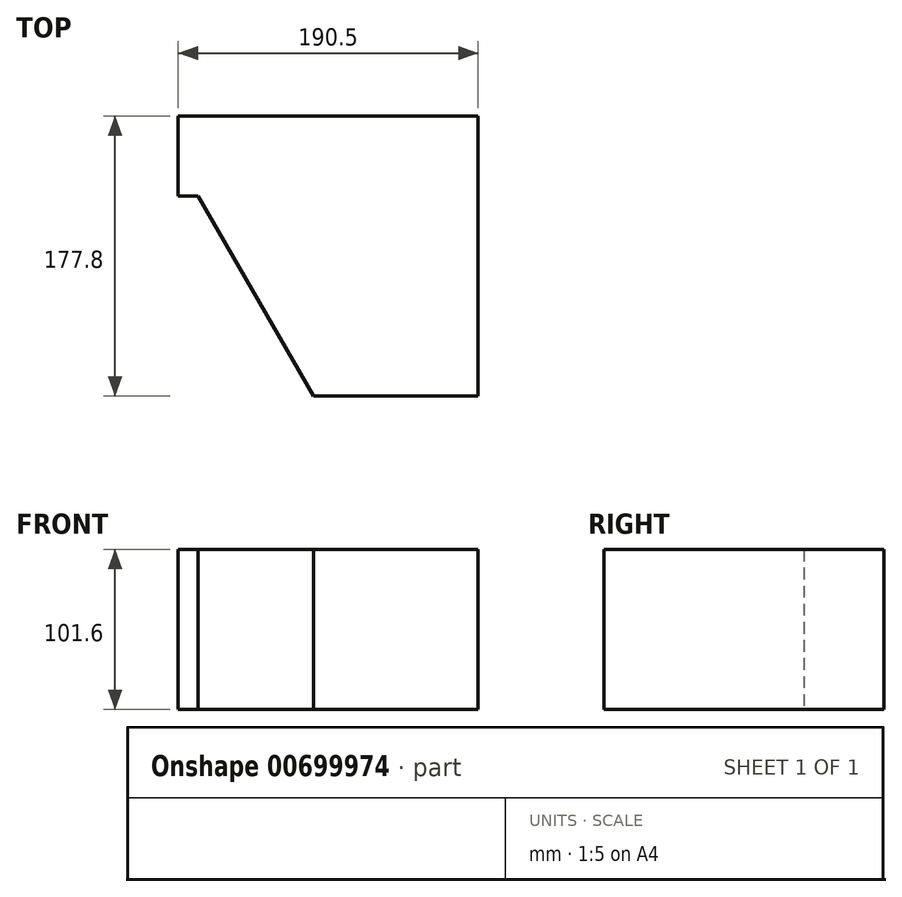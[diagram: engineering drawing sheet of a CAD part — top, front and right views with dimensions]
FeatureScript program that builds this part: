
annotation { "Feature Type Name" : "Feature", "Feature Type Description" : "" }
export const myFeature = defineFeature(function(context is Context, id is Id, definition is map)
    precondition{}
    {
        {
            var Q0;
            Q0=qCreatedBy(makeId("Front.planeOp"),FACE);
            var sketch = newSketch(context, id + "F0", { "sketchPlane" : qUnion([Q0])});
            skLineSegment(sketch, "E0.bottom", {"start": v(-95.25, 50.8) * mm, "end": v(95.25, 50.8) * mm});
            skLineSegment(sketch, "E0.top", {"start": v(-95.25, -50.8) * mm, "end": v(95.25, -50.8) * mm});
            skLineSegment(sketch, "E0.left", {"start": v(-95.25, 50.8) * mm, "end": v(-95.25, -50.8) * mm});
            skLineSegment(sketch, "E0.right", {"start": v(95.25, 50.8) * mm, "end": v(95.25, -50.8) * mm});
            skPoint(sketch, "E0.middle", {"position": v(0, 0) * mm});
            skSolve(sketch);
        }
        {
            var Q0;
            Q0 = qSketchRegion(id + "F0", true);
            var Q1;
            Q1=makeQuery(id+"F0.imprint","IMPRINT",FACE,{"disambiguationData":[TD([[makeQuery(id+"F0.imprint","IMPRINT",EDGE,{"derivedFrom":sQuery(id+"F0.wireOp",EDGE,"E0.bottom")}),-1.0]])]});
            extrude(context, id + "F1", {"entities" : qUnion([Q0, Q1]), "depth" : 177.8 * mm, "offsetDistance" : 25.4 * mm});
        }
        {
            var Q0;
            Q0=makeQuery(id+"F1.opExtrude","SWEPT_FACE",FACE,{"disambiguationData":[OSD([sQuery(id+"F0.wireOp",EDGE,"E0.top")])]});
            var sketch = newSketch(context, id + "F2", { "sketchPlane" : qUnion([Q0])});
            skLineSegment(sketch, "E1", {"start": v(-95.25, 50.8) * mm, "end": v(-82.55, 50.8) * mm});
            skLineSegment(sketch, "E2", {"start": v(-82.55, 50.8) * mm, "end": v(-9.23, 177.8) * mm});
            skLineSegment(sketch, "E3", {"start": v(-95.25, 50.8) * mm, "end": v(-95.25, 177.8) * mm});
            skLineSegment(sketch, "E4", {"start": v(-95.25, 177.8) * mm, "end": v(-9.23, 177.8) * mm});
            skSolve(sketch);
        }
        {
            var Q0;
            Q0 = qSketchRegion(id + "F2", true);
            extrude(context, id + "F3", {"entities" : qUnion([Q0]), "operationType" : NewBodyOperationType.REMOVE, "endBound" : BoundingType.THROUGH_ALL, "oppositeDirection" : true, "depth" : 25.4 * mm, "offsetDistance" : 25.4 * mm});
        }
    });
